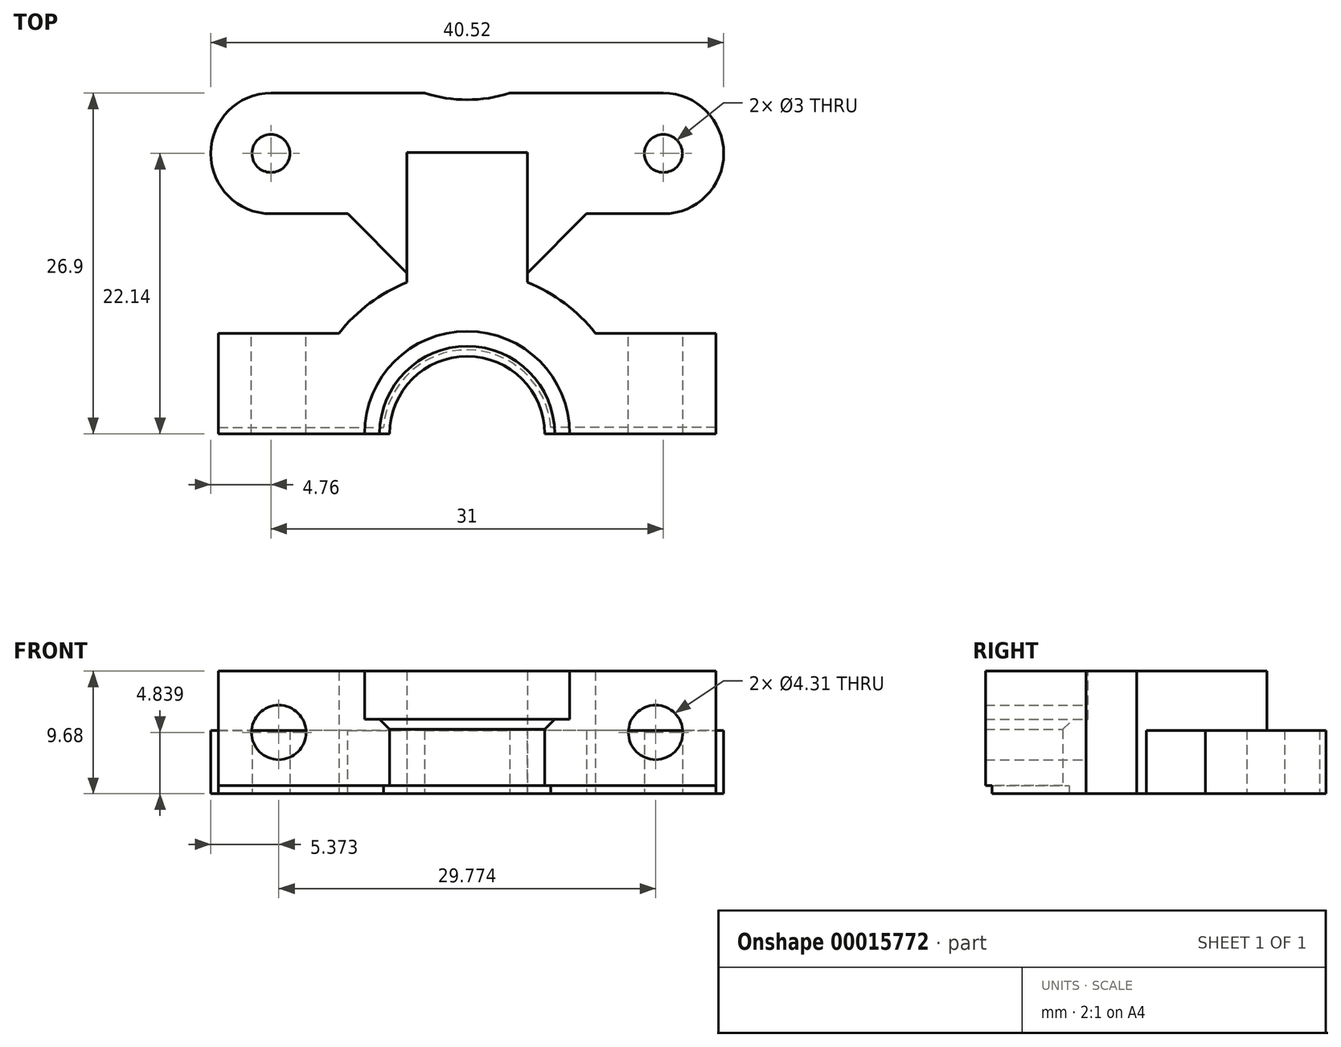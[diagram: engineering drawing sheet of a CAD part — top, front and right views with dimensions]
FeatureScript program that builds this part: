
annotation { "Feature Type Name" : "Feature", "Feature Type Description" : "" }
export const myFeature = defineFeature(function(context is Context, id is Id, definition is map)
    precondition{}
    {
        {
            var Q0;
            Q0=qCreatedBy(makeId("Top.planeOp"),FACE);
            var sketch = newSketch(context, id + "F0", { "sketchPlane" : qUnion([Q0])});
            skLineSegment(sketch, "E0", {"start": v(0, 0) * mm, "end": v(-31, 0) * mm, "construction": true});
            skLineSegment(sketch, "E1", {"start": v(-15.5, 0) * mm, "end": v(-15.5, 15.5) * mm, "construction": true});
            skCircle(sketch, "E2", {"center": v(0, 0) * mm, "radius": 1.5 * mm});
            skCircle(sketch, "E3", {"center": v(-31, 0) * mm, "radius": 1.5 * mm});
            skLineSegment(sketch, "E4.bottom", {"start": v(-10.74, -4.76) * mm, "end": v(-20.26, -4.76) * mm, "construction": true});
            skLineSegment(sketch, "E4.left", {"start": v(-10.74, -4.76) * mm, "end": v(-10.74, -10.19) * mm});
            skLineSegment(sketch, "E4.right", {"start": v(-20.26, -4.76) * mm, "end": v(-20.26, -10.19) * mm});
            skLineSegment(sketch, "E5.bottom", {"start": v(0, 4.76) * mm, "end": v(-12.13, 4.76) * mm});
            skLineSegment(sketch, "E5.top", {"start": v(0, -4.76) * mm, "end": v(-10.74, -4.76) * mm});
            skLineSegment(sketch, "E5.left", {"start": v(0, 4.76) * mm, "end": v(0, -4.76) * mm, "construction": true});
            skLineSegment(sketch, "E6.bottom", {"start": v(-20.26, -4.76) * mm, "end": v(-31, -4.76) * mm});
            skLineSegment(sketch, "E6.top", {"start": v(-18.87, 4.76) * mm, "end": v(-31, 4.76) * mm});
            skLineSegment(sketch, "E6.right", {"start": v(-31, -4.76) * mm, "end": v(-31, 4.76) * mm, "construction": true});
            skArc(sketch, "E7", {"start": v(0, -4.76) * mm, "mid": v(4.76, 0) * mm, "end": v(0, 4.76) * mm});
            skArc(sketch, "E8", {"start": v(-31, 4.76) * mm, "mid": v(-35.76, 0) * mm, "end": v(-31, -4.76) * mm});
            skArc(sketch, "E9", {"start": v(-18.87, 4.76) * mm, "mid": v(-15.5, 4.25) * mm, "end": v(-12.13, 4.76) * mm});
            skArc(sketch, "E10", {"start": v(-5.38, -14.2) * mm, "mid": v(-7.8, -11.84) * mm, "end": v(-10.74, -10.19) * mm});
            skArc(sketch, "E11", {"start": v(-20.26, -10.19) * mm, "mid": v(-23.2, -11.84) * mm, "end": v(-25.62, -14.2) * mm});
            skLineSegment(sketch, "E12", {"start": v(-15.5, -4.76) * mm, "end": v(-15.5, -22.14) * mm, "construction": true});
            skLineSegment(sketch, "E13", {"start": v(-5.38, -14.2) * mm, "end": v(4.15, -14.2) * mm});
            skLineSegment(sketch, "E14", {"start": v(4.15, -14.2) * mm, "end": v(4.15, -22.14) * mm});
            skLineSegment(sketch, "E15", {"start": v(4.15, -22.14) * mm, "end": v(-9.38, -22.14) * mm});
            skLineSegment(sketch, "E16", {"start": v(-25.62, -14.2) * mm, "end": v(-35.15, -14.2) * mm});
            skLineSegment(sketch, "E17", {"start": v(-35.15, -14.2) * mm, "end": v(-35.15, -22.14) * mm});
            skLineSegment(sketch, "E18", {"start": v(-35.15, -22.14) * mm, "end": v(-21.62, -22.14) * mm});
            skArc(sketch, "E19", {"start": v(-9.38, -22.14) * mm, "mid": v(-15.5, -16.02) * mm, "end": v(-21.62, -22.14) * mm});
            skLineSegment(sketch, "E20", {"start": v(-9.38, -22.14) * mm, "end": v(-21.62, -22.14) * mm, "construction": true});
            skSolve(sketch);
        }
        {
            var Q0;
            Q0 = qSketchRegion(id + "F0", true);
            extrude(context, id + "F1", {"entities" : qUnion([Q0]), "depth" : 5 * mm});
        }
        {
            var Q0;
            Q0=makeQuery(id+"F1.opExtrude","CAP_FACE",FACE,{"disambiguationData":[OSD([sQuery(id+"F0.wireOp",EDGE,"E2"),sQuery(id+"F0.wireOp",EDGE,"E3"),sQuery(id+"F0.wireOp",EDGE,"E4.top"),sQuery(id+"F0.wireOp",EDGE,"E4.left"),sQuery(id+"F0.wireOp",EDGE,"E4.right"),sQuery(id+"F0.wireOp",EDGE,"E5.bottom"),sQuery(id+"F0.wireOp",EDGE,"E5.top"),sQuery(id+"F0.wireOp",EDGE,"E6.bottom"),sQuery(id+"F0.wireOp",EDGE,"E6.top"),sQuery(id+"F0.wireOp",EDGE,"E7"),sQuery(id+"F0.wireOp",EDGE,"E8"),sQuery(id+"F0.wireOp",EDGE,"E9")])],"isStart":false});
            var sketch = newSketch(context, id + "F2", { "sketchPlane" : qUnion([Q0])});
            skLineSegment(sketch, "E21.bottom", {"start": v(-10.74, 0.09) * mm, "end": v(-20.26, 0.09) * mm});
            skLineSegment(sketch, "E21.left", {"start": v(-10.74, 0.09) * mm, "end": v(-10.74, -10.19) * mm});
            skLineSegment(sketch, "E21.right", {"start": v(-20.26, 0.09) * mm, "end": v(-20.26, -10.19) * mm});
            skLineSegment(sketch, "E22", {"start": v(-15.5, 4.76) * mm, "end": v(-15.5, 0.09) * mm, "construction": true});
            skLineSegment(sketch, "E23", {"start": v(-12.13, 4.76) * mm, "end": v(-18.87, 4.76) * mm, "construction": true});
            skArc(sketch, "E24", {"start": v(-20.26, -10.19) * mm, "mid": v(-23.2, -11.84) * mm, "end": v(-25.62, -14.2) * mm});
            skArc(sketch, "E25", {"start": v(-5.38, -14.2) * mm, "mid": v(-7.8, -11.84) * mm, "end": v(-10.74, -10.19) * mm});
            skArc(sketch, "E26", {"start": v(-9.38, -22.14) * mm, "mid": v(-15.5, -16.02) * mm, "end": v(-21.62, -22.14) * mm});
            skLineSegment(sketch, "E27.bottom", {"start": v(-25.62, -14.2) * mm, "end": v(-35.15, -14.2) * mm});
            skLineSegment(sketch, "E27.top", {"start": v(-21.62, -22.14) * mm, "end": v(-35.15, -22.14) * mm});
            skLineSegment(sketch, "E27.right", {"start": v(-35.15, -14.2) * mm, "end": v(-35.15, -22.14) * mm});
            skLineSegment(sketch, "E28.bottom", {"start": v(-5.38, -14.2) * mm, "end": v(4.15, -14.2) * mm});
            skLineSegment(sketch, "E28.top", {"start": v(-9.38, -22.14) * mm, "end": v(4.15, -22.14) * mm});
            skLineSegment(sketch, "E28.right", {"start": v(4.15, -14.2) * mm, "end": v(4.15, -22.14) * mm});
            skSolve(sketch);
        }
        {
            var Q0;
            Q0 = qSketchRegion(id + "F2", true);
            extrude(context, id + "F3", {"entities" : qUnion([Q0]), "operationType" : NewBodyOperationType.ADD, "depth" : 4.68 * mm});
        }
        {
            var Q0;
            Q0=makeQuery(id+"F3.opExtrude","CAP_EDGE",EDGE,{"disambiguationData":[OSD([sQuery(id+"F2.wireOp",EDGE,"E21.bottom")])],"isStart":true});
            var Q1;
            Q1=makeQuery(id+"F3.opExtrude","CAP_EDGE",EDGE,{"disambiguationData":[OSD([sQuery(id+"F2.wireOp",EDGE,"E21.right")])],"isStart":true});
            var Q2;
            Q2=makeQuery(id+"F3.opExtrude","CAP_EDGE",EDGE,{"disambiguationData":[OSD([sQuery(id+"F2.wireOp",EDGE,"E21.left")])],"isStart":true});
            var Q3;
            Q3=makeQuery(id+"F1.opExtrude","SWEPT_EDGE",EDGE,{"disambiguationData":[OSD([sQuery(id+"F0.wireOp",EDGE,"E4.left"),sQuery(id+"F0.wireOp",EDGE,"E5.top")])]});
            var Q4;
            Q4=makeQuery(id+"F1.opExtrude","SWEPT_EDGE",EDGE,{"disambiguationData":[OSD([sQuery(id+"F0.wireOp",EDGE,"E4.right"),sQuery(id+"F0.wireOp",EDGE,"E6.bottom")])]});
            chamfer(context, id + "F4", {"entities" : qUnion([Q0, Q1, Q2, Q3, Q4]), "width" : 4.68 * mm, "tangentPropagation" : true});
        }
        {
            var Q0;
            Q0=makeQuery(id+"F3.opExtrude","CAP_FACE",FACE,{"disambiguationData":[OSD([sQuery(id+"F2.wireOp",EDGE,"E21.bottom"),sQuery(id+"F2.wireOp",EDGE,"E21.left"),sQuery(id+"F2.wireOp",EDGE,"E21.right"),sQuery(id+"F2.wireOp",EDGE,"E24"),sQuery(id+"F2.wireOp",EDGE,"E25"),sQuery(id+"F2.wireOp",EDGE,"E26"),sQuery(id+"F2.wireOp",EDGE,"E27.bottom"),sQuery(id+"F2.wireOp",EDGE,"E27.top"),sQuery(id+"F2.wireOp",EDGE,"E27.right"),sQuery(id+"F2.wireOp",EDGE,"E28.bottom"),sQuery(id+"F2.wireOp",EDGE,"E28.top"),sQuery(id+"F2.wireOp",EDGE,"E28.right")])],"isStart":false});
            var sketch = newSketch(context, id + "F5", { "sketchPlane" : qUnion([Q0])});
            skArc(sketch, "E29", {"start": v(-7.4, -22.14) * mm, "mid": v(-15.5, -14.04) * mm, "end": v(-23.6, -22.14) * mm});
            skLineSegment(sketch, "E30", {"start": v(-23.6, -22.14) * mm, "end": v(-7.4, -22.14) * mm});
            skSolve(sketch);
        }
        {
            var Q0;
            Q0 = qSketchRegion(id + "F5", true);
            extrude(context, id + "F6", {"entities" : qUnion([Q0]), "operationType" : NewBodyOperationType.REMOVE, "oppositeDirection" : true, "depth" : 3.8 * mm});
        }
        {
            var Q0;
            Q0=makeQuery(id+"F3.boolean.opBoolean","MERGE",FACE,{"derivedFrom":[makeQuery(id+"F1.opExtrude","SWEPT_FACE",FACE,{"disambiguationData":[OSD([sQuery(id+"F0.wireOp",EDGE,"E13")])]}),makeQuery(id+"F3.opExtrude","SWEPT_FACE",FACE,{"disambiguationData":[OSD([sQuery(id+"F2.wireOp",EDGE,"E28.bottom")])]})]});
            var sketch = newSketch(context, id + "F7", { "sketchPlane" : qUnion([Q0])});
            skLineSegment(sketch, "E31", {"start": v(-4.15, 4.84) * mm, "end": v(0.61, 4.84) * mm, "construction": true});
            skLineSegment(sketch, "E32", {"start": v(0.61, 4.84) * mm, "end": v(30.39, 4.84) * mm, "construction": true});
            skLineSegment(sketch, "E33", {"start": v(30.39, 4.84) * mm, "end": v(35.15, 4.84) * mm, "construction": true});
            skCircle(sketch, "E34", {"center": v(0.61, 4.84) * mm, "radius": 2.15 * mm});
            skCircle(sketch, "E35", {"center": v(30.39, 4.84) * mm, "radius": 2.15 * mm});
            skSolve(sketch);
        }
        {
            var Q0;
            Q0 = qSketchRegion(id + "F7", true);
            var Q1;
            Q1=makeQuery(id+"F3.boolean.opBoolean","MERGE",FACE,{"derivedFrom":[makeQuery(id+"F1.opExtrude","SWEPT_FACE",FACE,{"disambiguationData":[OSD([sQuery(id+"F0.wireOp",EDGE,"E15")])]}),makeQuery(id+"F3.opExtrude","SWEPT_FACE",FACE,{"disambiguationData":[OSD([sQuery(id+"F2.wireOp",EDGE,"E28.top")])]})]});
            extrude(context, id + "F8", {"entities" : qUnion([Q0]), "operationType" : NewBodyOperationType.REMOVE, "endBound" : BoundingType.UP_TO_SURFACE, "oppositeDirection" : true, "endBoundEntityFace" : qUnion([Q1]), "depth" : 25.4 * mm});
        }
        {
            var Q0;
            Q0=makeQuery(id+"F6.boolean.opBoolean","INTERSECT",EDGE,{"derivedFrom":[makeQuery(id+"F3.boolean.opBoolean","MERGE",FACE,{"derivedFrom":[makeQuery(id+"F1.opExtrude","SWEPT_FACE",FACE,{"disambiguationData":[OSD([sQuery(id+"F0.wireOp",EDGE,"E19")])]}),makeQuery(id+"F3.opExtrude","SWEPT_FACE",FACE,{"disambiguationData":[OSD([sQuery(id+"F2.wireOp",EDGE,"E26")])]})]}),makeQuery(id+"F6.opExtrude","CAP_FACE",FACE,{"disambiguationData":[OSD([sQuery(id+"F5.wireOp",EDGE,"E29"),sQuery(id+"F5.wireOp",EDGE,"E30")])],"isStart":false})]});
            chamfer(context, id + "F9", {"entities" : qUnion([Q0]), "width" : 0.8 * mm, "tangentPropagation" : true});
        }
        {
            var Q0;
            Q0=makeQuery(id+"F1.opExtrude","CAP_FACE",FACE,{"disambiguationData":[OSD([sQuery(id+"F0.wireOp",EDGE,"E2"),sQuery(id+"F0.wireOp",EDGE,"E3"),sQuery(id+"F0.wireOp",EDGE,"E4.left"),sQuery(id+"F0.wireOp",EDGE,"E4.right"),sQuery(id+"F0.wireOp",EDGE,"E5.bottom"),sQuery(id+"F0.wireOp",EDGE,"E5.top"),sQuery(id+"F0.wireOp",EDGE,"E6.bottom"),sQuery(id+"F0.wireOp",EDGE,"E6.top"),sQuery(id+"F0.wireOp",EDGE,"E7"),sQuery(id+"F0.wireOp",EDGE,"E8"),sQuery(id+"F0.wireOp",EDGE,"E9"),sQuery(id+"F0.wireOp",EDGE,"E10"),sQuery(id+"F0.wireOp",EDGE,"E11"),sQuery(id+"F0.wireOp",EDGE,"E13"),sQuery(id+"F0.wireOp",EDGE,"E14"),sQuery(id+"F0.wireOp",EDGE,"E15"),sQuery(id+"F0.wireOp",EDGE,"E16"),sQuery(id+"F0.wireOp",EDGE,"E17"),sQuery(id+"F0.wireOp",EDGE,"E18"),sQuery(id+"F0.wireOp",EDGE,"E19")])],"isStart":true});
            var sketch = newSketch(context, id + "F10", { "sketchPlane" : qUnion([Q0])});
            skLineSegment(sketch, "E36.bottom", {"start": v(-35.15, 22.14) * mm, "end": v(-21.62, 22.14) * mm});
            skLineSegment(sketch, "E36.top", {"start": v(-35.15, 21.63) * mm, "end": v(-22.1, 21.63) * mm});
            skLineSegment(sketch, "E36.left", {"start": v(-35.15, 22.14) * mm, "end": v(-35.15, 21.63) * mm});
            skLineSegment(sketch, "E37.bottom", {"start": v(4.15, 22.14) * mm, "end": v(-9.38, 22.14) * mm});
            skLineSegment(sketch, "E37.top", {"start": v(4.15, 21.63) * mm, "end": v(-8.9, 21.63) * mm});
            skLineSegment(sketch, "E37.left", {"start": v(4.15, 22.14) * mm, "end": v(4.15, 21.63) * mm});
            skArc(sketch, "E38", {"start": v(-21.62, 22.14) * mm, "mid": v(-15.5, 16.02) * mm, "end": v(-9.38, 22.14) * mm});
            skArc(sketch, "E39", {"start": v(-22.1, 21.63) * mm, "mid": v(-15.5, 15.51) * mm, "end": v(-8.9, 21.63) * mm});
            skSolve(sketch);
        }
        {
            var Q0;
            Q0 = qSketchRegion(id + "F10", true);
            extrude(context, id + "F11", {"entities" : qUnion([Q0]), "operationType" : NewBodyOperationType.REMOVE, "oppositeDirection" : true, "depth" : 0.64 * mm});
        }
    });
